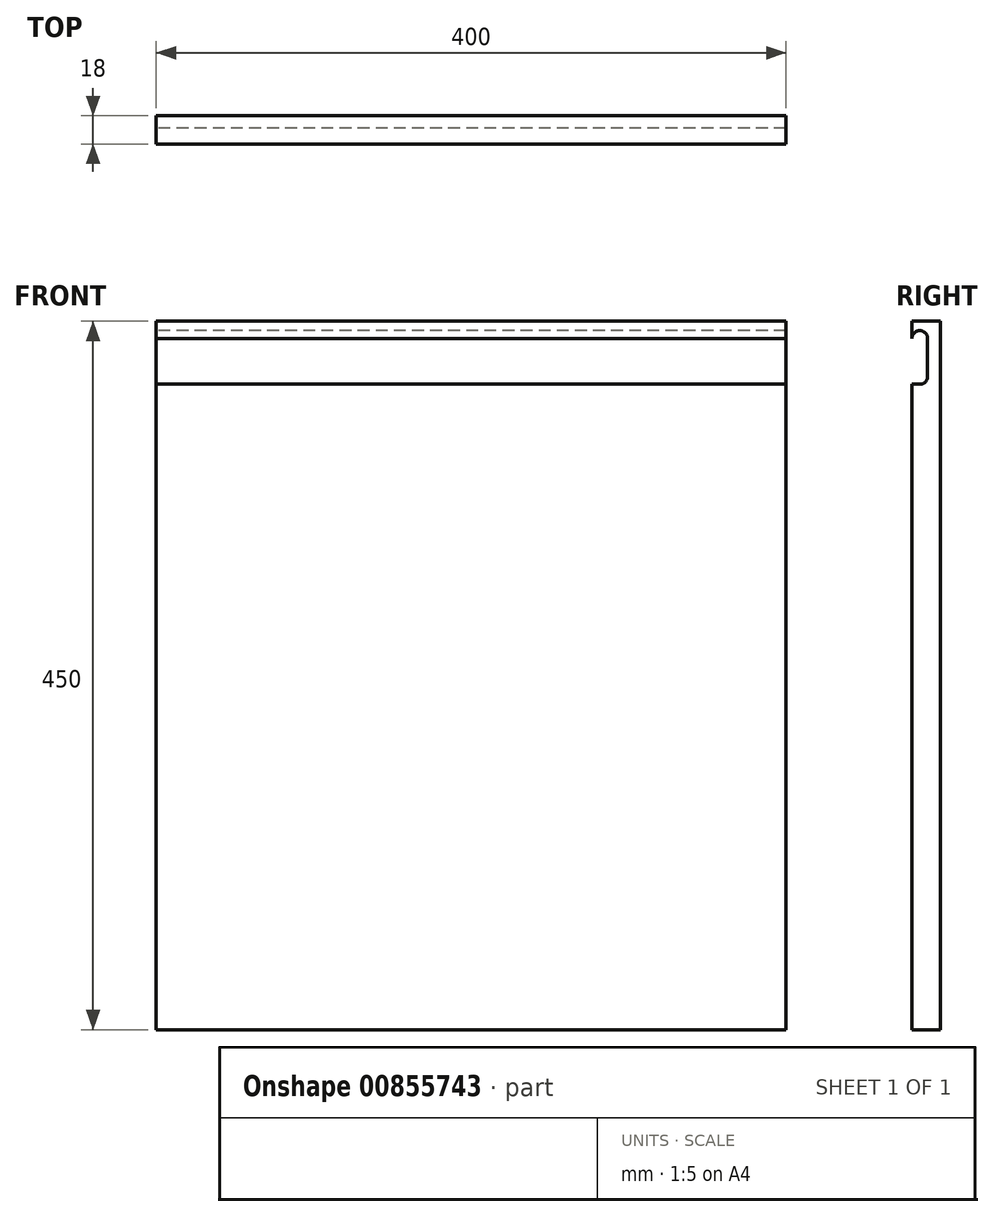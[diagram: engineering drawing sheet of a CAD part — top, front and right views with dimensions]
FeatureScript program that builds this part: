
annotation { "Feature Type Name" : "Feature", "Feature Type Description" : "" }
export const myFeature = defineFeature(function(context is Context, id is Id, definition is map)
    precondition{}
    {
        {
            var Q0;
            Q0=qCreatedBy(makeId("Front.planeOp"),FACE);
            var sketch = newSketch(context, id + "F0", { "sketchPlane" : qUnion([Q0])});
            skLineSegment(sketch, "E0.2", {"start": v(148.4, 210.16) * mm, "end": v(148.4, -203.84) * mm, "construction": true});
            skLineSegment(sketch, "E1", {"start": v(148.4, 210.16) * mm, "end": v(-208.6, 210.16) * mm, "construction": true});
            skLineSegment(sketch, "E2", {"start": v(-208.6, -203.84) * mm, "end": v(148.4, -203.84) * mm, "construction": true});
            skLineSegment(sketch, "E3.trimOffspring", {"start": v(-208.6, 210.16) * mm, "end": v(-208.6, -203.84) * mm, "construction": true});
            skLineSegment(sketch, "E4", {"start": v(-226.6, -221.84) * mm, "end": v(-226.6, 228.16) * mm});
            skLineSegment(sketch, "E5", {"start": v(-226.6, 228.16) * mm, "end": v(173.4, 228.16) * mm});
            skLineSegment(sketch, "E6", {"start": v(173.4, 228.16) * mm, "end": v(173.4, -221.84) * mm});
            skLineSegment(sketch, "E7", {"start": v(173.4, -221.84) * mm, "end": v(-226.6, -221.84) * mm});
            skSolve(sketch);
        }
        {
            var Q0;
            Q0=makeQuery(id+"F0.imprint","IMPRINT",FACE,{"disambiguationData":[TD([[makeQuery(id+"F0.imprint","IMPRINT",EDGE,{"derivedFrom":sQuery(id+"F0.wireOp",EDGE,"E4")}),-1.0]])]});
            extrude(context, id + "F1", {"entities" : qUnion([Q0]), "depth" : 18 * mm, "offsetDistance" : 25 * mm});
        }
        {
            var Q0;
            Q0=makeQuery(id+"F1.opExtrude","SWEPT_FACE",FACE,{"disambiguationData":[OSD([sQuery(id+"F0.wireOp",EDGE,"E4")])]});
            var sketch = newSketch(context, id + "F2", { "sketchPlane" : qUnion([Q0])});
            skLineSegment(sketch, "E8", {"start": v(18, 188.16) * mm, "end": v(13, 188.16) * mm});
            skLineSegment(sketch, "E9", {"start": v(8, 193.16) * mm, "end": v(8, 217.16) * mm});
            skArc(sketch, "E10", {"start": v(18, 217.16) * mm, "mid": v(13, 222.16) * mm, "end": v(8, 217.16) * mm});
            skPoint(sketch, "E11.visualSharp", {"position": v(8, 188.16) * mm});
            skArc(sketch, "E11.filletArc", {"start": v(8, 193.16) * mm, "mid": v(9.46, 189.62) * mm, "end": v(13, 188.16) * mm});
            skSolve(sketch);
        }
        {
            var Q0;
            {var subQ1=sQuery(id+"F2.wireOp",EDGE,"E8");Q0=makeQuery(id+"F2.imprint","IMPRINT",FACE,{"disambiguationData":[TD([[makeQuery(id+"F2.imprint","IMPRINT",EDGE,{"derivedFrom":subQ1}),-1.0]])]});}
            extrude(context, id + "F3", {"entities" : qUnion([Q0]), "operationType" : NewBodyOperationType.REMOVE, "oppositeDirection" : true, "depth" : 522.8 * mm, "offsetDistance" : 25 * mm});
        }
    });
